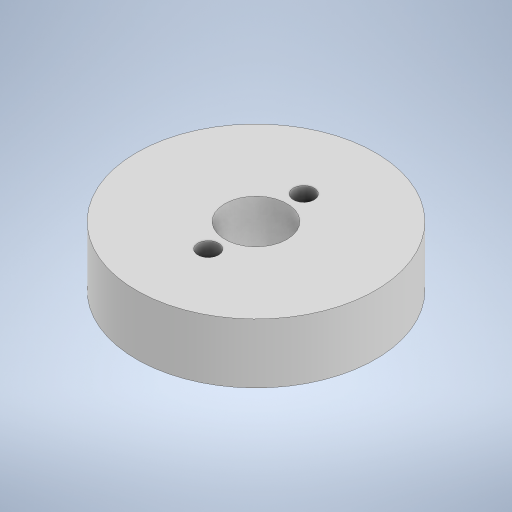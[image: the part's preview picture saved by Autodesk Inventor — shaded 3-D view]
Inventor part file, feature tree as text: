
AUTODESK INVENTOR PART (.ipt)
format: ipt  version: 2024.2 (Build 282272000, 272)  size: 232,960 bytes
history: native  units: in
note: dims shown in document units (in); Inventor stores cm internally (conversion verified against a paired STEP export)
features: extrude x3, sketch x3
ambient origin geometry x8: Origin, YZ Plane, XZ Plane, XY Plane, X Axis, Y Axis, Z Axis, Center Point
bodies: Solid1 (feature_tree)
feature tree (6):
  extrude  "Extrusion1"  Depth=0.26in
  extrude  "Extrusion2"  Depth=0.25in
  extrude  "Extrusion3"  Depth=0.087in
  sketch  "Sketch1"  dims[d0=1.0in d1=0.26in]
  sketch  "Sketch2"  dims[d2=0.25in d3=0.0in d4=0.2in]
  sketch  "Sketch3"  dims[d5=0.2in d6=0.087in d7=0.087in d8=0.175in d9=0.0in d10=0.2in d11=0.4in d12=0.075in d13=0.0in d14=0.087in d15=0.087in]
